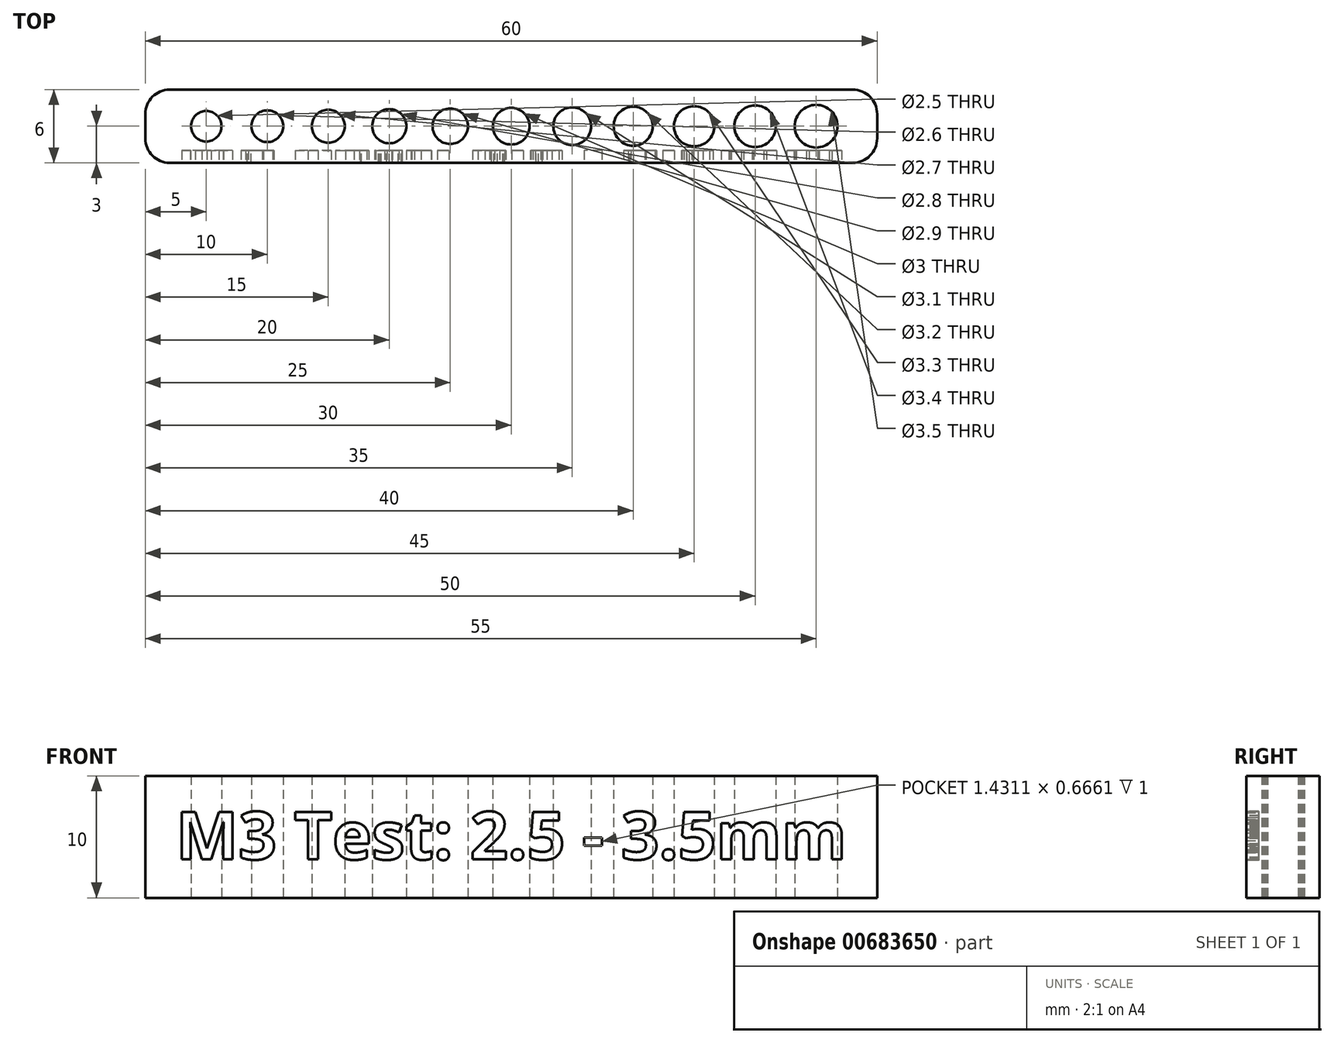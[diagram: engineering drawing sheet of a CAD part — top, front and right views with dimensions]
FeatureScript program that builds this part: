
annotation { "Feature Type Name" : "Feature", "Feature Type Description" : "" }
export const myFeature = defineFeature(function(context is Context, id is Id, definition is map)
    precondition{}
    {
        {
            var Q0;
            Q0=qCreatedBy(makeId("Top.planeOp"),FACE);
            var sketch = newSketch(context, id + "F0", { "sketchPlane" : qUnion([Q0])});
            skLineSegment(sketch, "E0.bottom", {"start": v(-30, 3) * mm, "end": v(30, 3) * mm});
            skLineSegment(sketch, "E0.top", {"start": v(-30, -3) * mm, "end": v(30, -3) * mm});
            skLineSegment(sketch, "E0.left", {"start": v(-30, 3) * mm, "end": v(-30, -3) * mm});
            skLineSegment(sketch, "E0.right", {"start": v(30, 3) * mm, "end": v(30, -3) * mm});
            skCircle(sketch, "E1", {"center": v(-25, 0) * mm, "radius": 1.25 * mm});
            skCircle(sketch, "E2", {"center": v(-20, 0) * mm, "radius": 1.3 * mm});
            skCircle(sketch, "E3", {"center": v(-15, 0) * mm, "radius": 1.35 * mm});
            skCircle(sketch, "E4", {"center": v(-10, 0) * mm, "radius": 1.4 * mm});
            skCircle(sketch, "E5", {"center": v(-5, 0) * mm, "radius": 1.45 * mm});
            skCircle(sketch, "E6", {"center": v(0, 0) * mm, "radius": 1.5 * mm});
            skCircle(sketch, "E7", {"center": v(5, 0) * mm, "radius": 1.55 * mm});
            skCircle(sketch, "E8", {"center": v(10, 0) * mm, "radius": 1.6 * mm});
            skCircle(sketch, "E9", {"center": v(15, 0) * mm, "radius": 1.65 * mm});
            skCircle(sketch, "E10", {"center": v(20, 0) * mm, "radius": 1.7 * mm});
            skCircle(sketch, "E11", {"center": v(25, 0) * mm, "radius": 1.75 * mm});
            skSolve(sketch);
        }
        {
            var Q0;
            Q0 = qSketchRegion(id + "F0", true);
            extrude(context, id + "F1", {"entities" : qUnion([Q0]), "depth" : 10 * mm, "offsetDistance" : 25 * mm});
        }
        {
            var Q0;
            Q0=makeQuery(id+"F1.opExtrude","SWEPT_EDGE",EDGE,{"disambiguationData":[OSD([sQuery(id+"F0.wireOp",EDGE,"E0.top"),sQuery(id+"F0.wireOp",EDGE,"E0.left")])]});
            var Q1;
            Q1=makeQuery(id+"F1.opExtrude","SWEPT_EDGE",EDGE,{"disambiguationData":[OSD([sQuery(id+"F0.wireOp",EDGE,"E0.top"),sQuery(id+"F0.wireOp",EDGE,"E0.right")])]});
            var Q2;
            Q2=makeQuery(id+"F1.opExtrude","SWEPT_EDGE",EDGE,{"disambiguationData":[OSD([sQuery(id+"F0.wireOp",EDGE,"E0.bottom"),sQuery(id+"F0.wireOp",EDGE,"E0.right")])]});
            var Q3;
            Q3=makeQuery(id+"F1.opExtrude","SWEPT_EDGE",EDGE,{"disambiguationData":[OSD([sQuery(id+"F0.wireOp",EDGE,"E0.bottom"),sQuery(id+"F0.wireOp",EDGE,"E0.left")])]});
            fillet(context, id + "F2", {"entities" : qUnion([Q0, Q1, Q2, Q3]), "radius" : 2 * mm, "tangentPropagation" : true, "allowEdgeOverflow" : false});
        }
        {
            var Q0;
            Q0=makeQuery(id+"F1.opExtrude","SWEPT_FACE",FACE,{"disambiguationData":[OSD([sQuery(id+"F0.wireOp",EDGE,"E0.top")])]});
            var sketch = newSketch(context, id + "F3", { "sketchPlane" : qUnion([Q0])});
            skText(sketch, "E12", { "text": "M3 Test: 2.5 - 3.5mm", "fontName": "OpenSans-Bold.ttf"});
            const initialGuessF3  = {"E12": [-0.0275, 0.00315, 1, 0, 0.00393]};
            skSetInitialGuess(sketch, initialGuessF3);
            skSolve(sketch);
        }
        {
            var Q0;
            Q0 = qSketchRegion(id + "F3", true);
            extrude(context, id + "F4", {"entities" : qUnion([Q0]), "operationType" : NewBodyOperationType.REMOVE, "oppositeDirection" : true, "depth" : 1 * mm, "offsetDistance" : 25 * mm});
        }
    });
